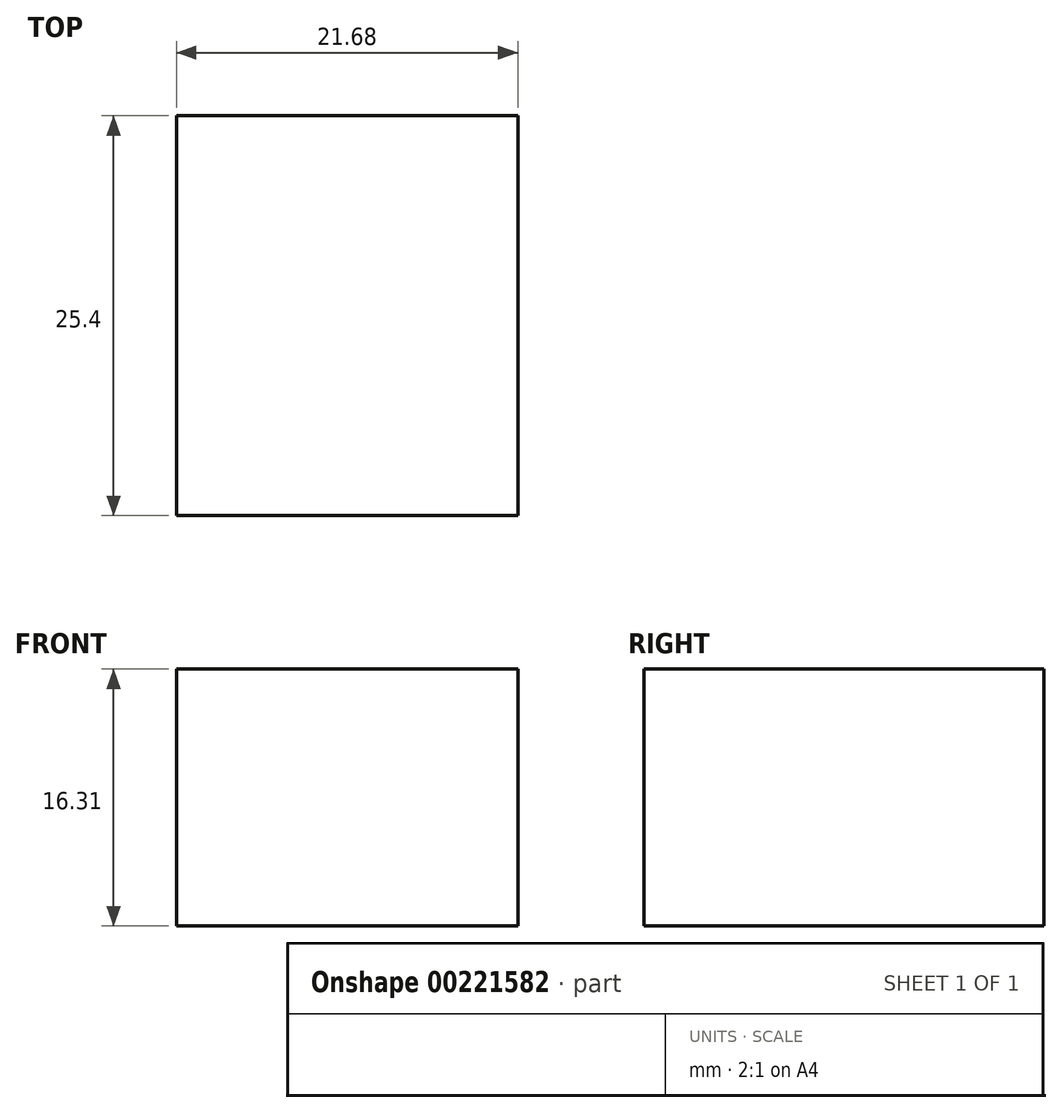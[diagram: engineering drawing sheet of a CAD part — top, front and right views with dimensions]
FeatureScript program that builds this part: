
annotation { "Feature Type Name" : "Feature", "Feature Type Description" : "" }
export const myFeature = defineFeature(function(context is Context, id is Id, definition is map)
    precondition{}
    {
        {
            var Q0;
            Q0=qCreatedBy(makeId("Front.planeOp"),FACE);
            var sketch = newSketch(context, id + "F0", { "sketchPlane" : qUnion([Q0])});
            skLineSegment(sketch, "E0.bottom", {"start": v(0, 0) * mm, "end": v(21.68, 0) * mm});
            skLineSegment(sketch, "E0.top", {"start": v(0, 16.31) * mm, "end": v(21.68, 16.31) * mm});
            skLineSegment(sketch, "E0.left", {"start": v(0, 0) * mm, "end": v(0, 16.31) * mm});
            skLineSegment(sketch, "E0.right", {"start": v(21.68, 0) * mm, "end": v(21.68, 16.31) * mm});
            skSolve(sketch);
        }
        {
            var Q0;
            Q0=makeQuery(id+"F0.imprint","IMPRINT",FACE,{"disambiguationData":[TD([[makeQuery(id+"F0.imprint","IMPRINT",EDGE,{"derivedFrom":sQuery(id+"F0.wireOp",EDGE,"E0.bottom")}),1.0]])]});
            var Q1;
            Q1 = qSketchRegion(id + "F0", true);
            extrude(context, id + "F1", {"entities" : qUnion([Q0, Q1]), "depth" : 25.4 * mm});
        }
    });
